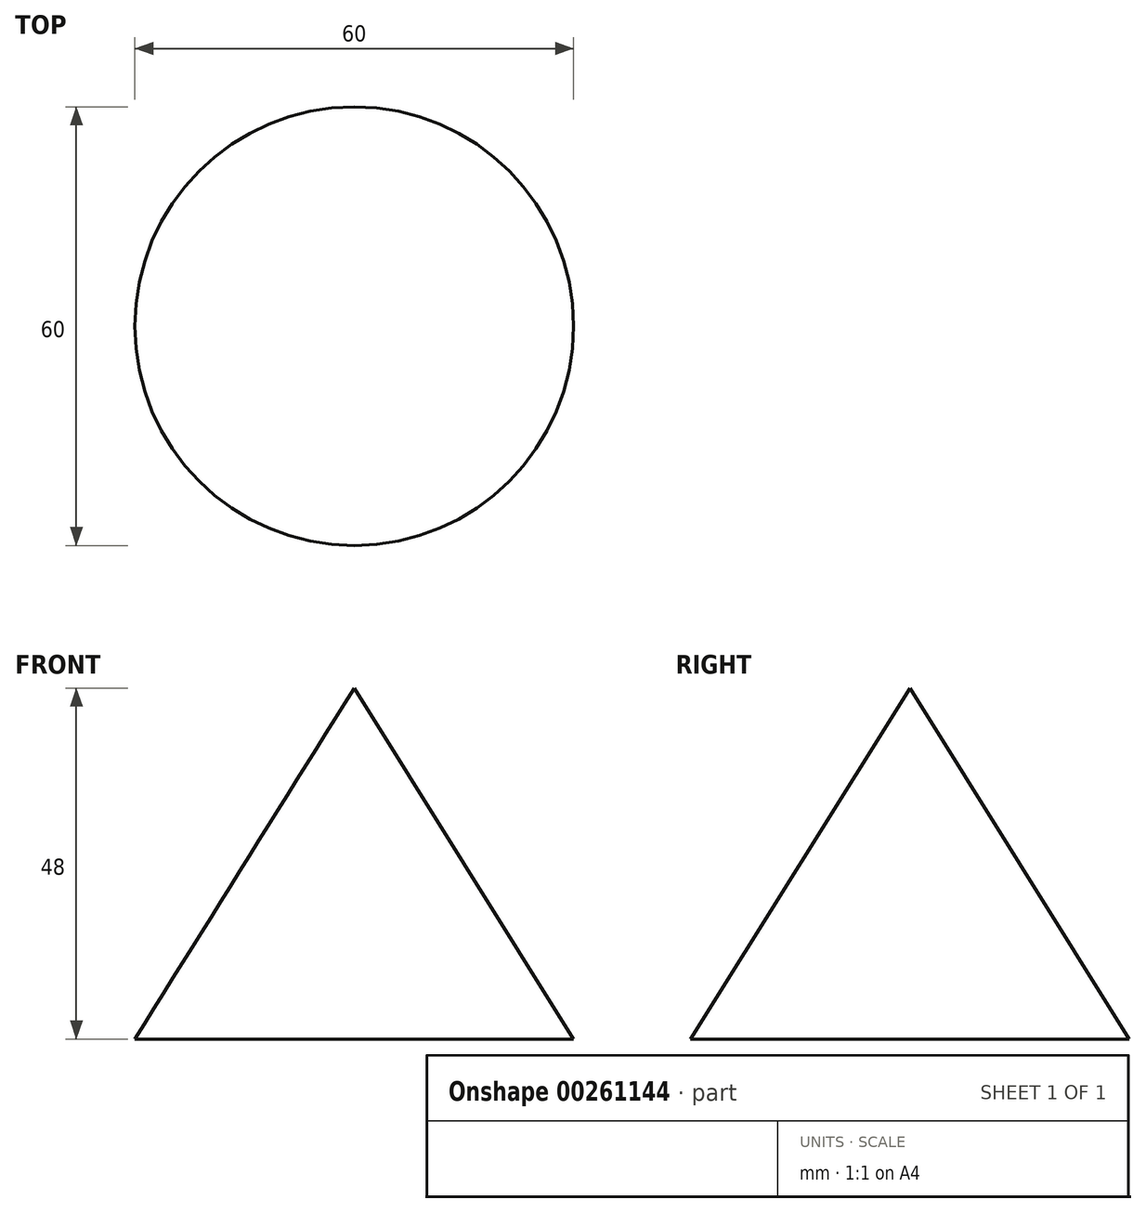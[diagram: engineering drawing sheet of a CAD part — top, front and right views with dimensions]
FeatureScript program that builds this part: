
annotation { "Feature Type Name" : "Feature", "Feature Type Description" : "" }
export const myFeature = defineFeature(function(context is Context, id is Id, definition is map)
    precondition{}
    {
        {
            var Q0;
            Q0=qCreatedBy(makeId("Front.planeOp"),FACE);
            var sketch = newSketch(context, id + "F0", { "sketchPlane" : qUnion([Q0])});
            skLineSegment(sketch, "E0", {"start": v(0, 0) * mm, "end": v(30, 0) * mm});
            skLineSegment(sketch, "E1", {"start": v(30, 0) * mm, "end": v(0, 48) * mm});
            skLineSegment(sketch, "E2", {"start": v(0, 48) * mm, "end": v(0, 0) * mm});
            skLineSegment(sketch, "E3", {"start": v(0, 59.78) * mm, "end": v(0, -32.5) * mm, "construction": true});
            skSolve(sketch);
        }
        {
            var Q0;
            Q0=makeQuery(id+"F0.imprint","IMPRINT",FACE,{"disambiguationData":[TD([[makeQuery(id+"F0.imprint","IMPRINT",EDGE,{"derivedFrom":sQuery(id+"F0.wireOp",EDGE,"E0")}),1.0]])]});
            var Q1;
            Q1=sQuery(id+"F0.wireOp",EDGE,"E3");
            revolve(context, id + "F1", {"entities" : qUnion([Q0]), "axis" : qUnion([Q1]), "revolveType" : RevolveType.FULL});
        }
    });
